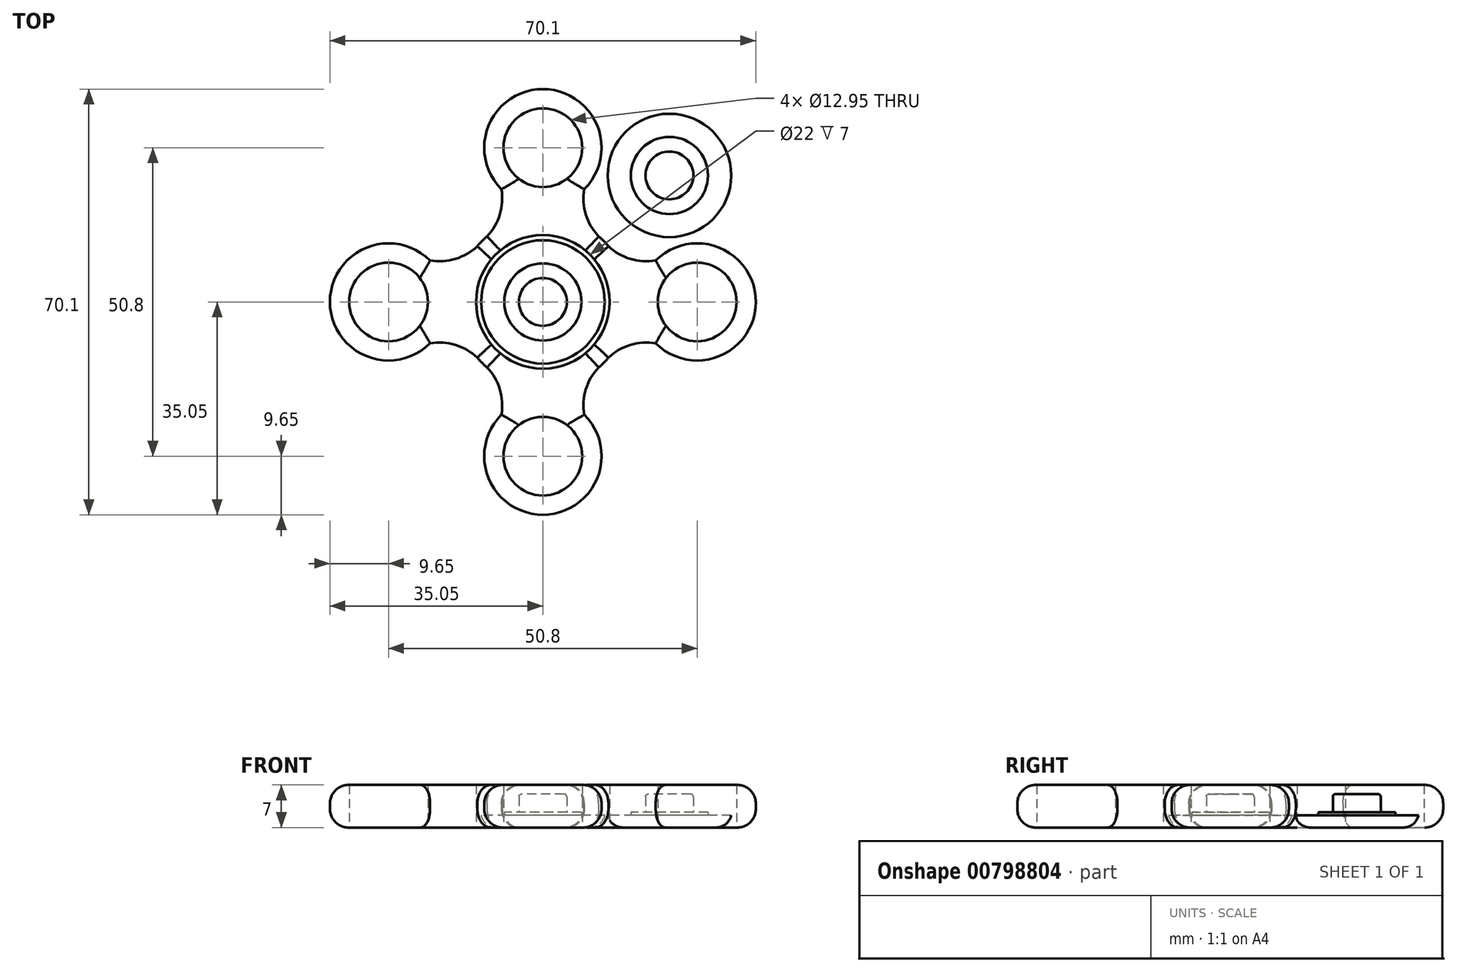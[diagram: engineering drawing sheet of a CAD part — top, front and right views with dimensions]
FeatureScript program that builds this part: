
annotation { "Feature Type Name" : "Feature", "Feature Type Description" : "" }
export const myFeature = defineFeature(function(context is Context, id is Id, definition is map)
    precondition{}
    {
        {
            var Q0;
            Q0=qCreatedBy(makeId("Top.planeOp"),FACE);
            var sketch = newSketch(context, id + "F0", { "sketchPlane" : qUnion([Q0])});
            skCircle(sketch, "E0", {"center": v(0, 0) * mm, "radius": 11 * mm});
            skCircle(sketch, "E1", {"center": v(0, 25.4) * mm, "radius": 6.48 * mm});
            skCircle(sketch, "E2", {"center": v(0, 0) * mm, "radius": 14.17 * mm});
            skCircle(sketch, "E3", {"center": v(0, 25.4) * mm, "radius": 9.65 * mm});
            skArc(sketch, "E4", {"start": v(-10.02, 10.02) * mm, "mid": v(-7.26, 13.86) * mm, "end": v(-6.82, 18.58) * mm});
            skArc(sketch, "E5", {"start": v(6.82, 18.58) * mm, "mid": v(7.26, 13.86) * mm, "end": v(10.02, 10.02) * mm});
            skCircle(sketch, "E6.1.0", {"center": v(-25.4, 0) * mm, "radius": 6.48 * mm});
            skCircle(sketch, "E6.1.1", {"center": v(-25.4, 0) * mm, "radius": 9.65 * mm});
            skArc(sketch, "E6.1.2", {"start": v(-18.58, 6.82) * mm, "mid": v(-13.86, 7.26) * mm, "end": v(-10.02, 10.02) * mm});
            skArc(sketch, "E6.1.3", {"start": v(-10.02, -10.02) * mm, "mid": v(-13.86, -7.26) * mm, "end": v(-18.58, -6.82) * mm});
            skCircle(sketch, "E6.2.0", {"center": v(0, -25.4) * mm, "radius": 6.48 * mm});
            skCircle(sketch, "E6.2.1", {"center": v(0, -25.4) * mm, "radius": 9.65 * mm});
            skArc(sketch, "E6.2.2", {"start": v(-6.82, -18.58) * mm, "mid": v(-7.26, -13.86) * mm, "end": v(-10.02, -10.02) * mm});
            skArc(sketch, "E6.2.3", {"start": v(10.02, -10.02) * mm, "mid": v(7.26, -13.86) * mm, "end": v(6.82, -18.58) * mm});
            skCircle(sketch, "E7.2.3.0", {"center": v(25.4, 0) * mm, "radius": 9.65 * mm});
            skArc(sketch, "E7.4.3.0", {"start": v(18.58, -6.82) * mm, "mid": v(13.86, -7.26) * mm, "end": v(10.02, -10.02) * mm});
            skArc(sketch, "E7.8.3.0", {"start": v(10.02, 10.02) * mm, "mid": v(13.86, 7.26) * mm, "end": v(18.58, 6.82) * mm});
            skCircle(sketch, "E7.10.3.0", {"center": v(25.4, 0) * mm, "radius": 6.48 * mm});
            skSolve(sketch);
        }
        {
            var Q0;
            Q0=qCreatedBy(makeId("Top.planeOp"),FACE);
            var sketch = newSketch(context, id + "F1", { "sketchPlane" : qUnion([Q0])});
            skCircle(sketch, "E8", {"center": v(0, 0) * mm, "radius": 10.16 * mm});
            skCircle(sketch, "E9", {"center": v(0, 0) * mm, "radius": 6.35 * mm});
            skCircle(sketch, "E10", {"center": v(0, 0) * mm, "radius": 3.94 * mm});
            skSolve(sketch);
        }
        {
            var Q0;
            Q0 = qSketchRegion(id + "F1", true);
            extrude(context, id + "F2", {"entities" : qUnion([Q0]), "depth" : 1.98 * mm, "offsetDistance" : 25.4 * mm});
        }
        {
            var Q0;
            Q0=makeQuery(id+"F1.imprint","IMPRINT",FACE,{"disambiguationData":[TD([[makeQuery(id+"F1.imprint","IMPRINT",EDGE,{"derivedFrom":sQuery(id+"F1.wireOp",EDGE,"E9")}),1.0]])]});
            extrude(context, id + "F3", {"entities" : qUnion([Q0]), "operationType" : NewBodyOperationType.ADD, "depth" : 2.5 * mm, "offsetDistance" : 25.4 * mm});
        }
        {
            var Q0;
            Q0=makeQuery(id+"F1.imprint","IMPRINT",FACE,{"disambiguationData":[TD([[makeQuery(id+"F1.imprint","IMPRINT",EDGE,{"derivedFrom":sQuery(id+"F1.wireOp",EDGE,"E10")}),1.0]])]});
            extrude(context, id + "F4", {"entities" : qUnion([Q0]), "operationType" : NewBodyOperationType.ADD, "depth" : 5.5 * mm, "offsetDistance" : 25.4 * mm});
        }
        {
            var Q0;
            {var subQ0=sQuery(id+"F1.wireOp",EDGE,"E10");var subQ1=sQuery(id+"F1.wireOp",EDGE,"E9");Q0=makeQuery(id+"F4.boolean.opBoolean","MERGE",FACE,{"derivedFrom":[makeQuery(id+"F3.boolean.opBoolean","MERGE",FACE,{"derivedFrom":[makeQuery(id+"F2.opExtrude","CAP_FACE",FACE,{"disambiguationData":[OSD([sQuery(id+"F1.wireOp",EDGE,"E8"),subQ1])],"isStart":true}),makeQuery(id+"F3.opExtrude","CAP_FACE",FACE,{"disambiguationData":[OSD([subQ1,subQ0])],"isStart":true})]}),makeQuery(id+"F4.opExtrude","CAP_FACE",FACE,{"disambiguationData":[OSD([subQ0])],"isStart":true})]});}
            fillet(context, id + "F5", {"entities" : qUnion([Q0]), "radius" : 2.54 * mm, "tangentPropagation" : true, "allowEdgeOverflow" : false});
        }
        {
            var Q0;
            Q0=makeQuery(id+"F4.opExtrude","CAP_EDGE",EDGE,{"disambiguationData":[OSD([sQuery(id+"F1.wireOp",EDGE,"E10")])],"isStart":false});
            fillet(context, id + "F6", {"entities" : qUnion([Q0]), "radius" : 0.43 * mm, "tangentPropagation" : true, "allowEdgeOverflow" : false});
        }
        {
            var Q0;
            Q0=makeQuery(id+"F2.opExtrude","SWEPT_BODY",BODY,{"disambiguationData":[OSD([sQuery(id+"F1.wireOp",EDGE,"E8"),sQuery(id+"F1.wireOp",EDGE,"E9")])]});
            transform(context, id + "F7", {"entities" : qUnion([Q0]), "transformType" : TransformType.TRANSLATION_3D, "dx" : 20.83 * mm, "dy" : 20.83 * mm, "dz" : 0 * mm, "makeCopy" : true});
        }
        {
            var Q0;
            Q0 = qSketchRegion(id + "F0", true);
            var Q1;
            Q1=makeQuery(id+"F0.imprint","IMPRINT",FACE,{"disambiguationData":[TD([[makeQuery(id+"F0.imprint","IMPRINT",EDGE,{"derivedFrom":sQuery(id+"F0.wireOp",EDGE,"E0")}),-1.0]])]});
            var Q2;
            {var subQ0=sQuery(id+"F0.wireOp",EDGE,"E6.2.2");var subQ1=sQuery(id+"F0.wireOp",EDGE,"E2");var subQ2=makeQuery(id+"F0.imprint","INTERSECT",VERTEX,{"disambiguationData":[OD(0.0)],"derivedFrom":[subQ1,subQ0]});Q2=makeQuery(id+"F0.imprint","IMPRINT",FACE,{"disambiguationData":[TD([[makeQuery(id+"F0.imprint","IMPRINT",EDGE,{"disambiguationData":[TD([[subQ2,-1.0]])],"derivedFrom":subQ1}),1.0]])]});}
            var Q3;
            {var subQ0=sQuery(id+"F0.wireOp",EDGE,"E6.1.3");var subQ1=sQuery(id+"F0.wireOp",EDGE,"E2");var subQ2=makeQuery(id+"F0.imprint","INTERSECT",VERTEX,{"disambiguationData":[OD(0.0)],"derivedFrom":[subQ1,subQ0]});Q3=makeQuery(id+"F0.imprint","IMPRINT",FACE,{"disambiguationData":[TD([[makeQuery(id+"F0.imprint","IMPRINT",EDGE,{"disambiguationData":[TD([[subQ2,1.0]])],"derivedFrom":subQ1}),1.0]])]});}
            var Q4;
            {var subQ0=sQuery(id+"F0.wireOp",EDGE,"E4");var subQ1=sQuery(id+"F0.wireOp",EDGE,"E2");var subQ2=makeQuery(id+"F0.imprint","INTERSECT",VERTEX,{"disambiguationData":[OD(0.0)],"derivedFrom":[subQ1,subQ0]});Q4=makeQuery(id+"F0.imprint","IMPRINT",FACE,{"disambiguationData":[TD([[makeQuery(id+"F0.imprint","IMPRINT",EDGE,{"disambiguationData":[TD([[subQ2,1.0]])],"derivedFrom":subQ1}),1.0]])]});}
            var Q5;
            {var subQ0=sQuery(id+"F0.wireOp",EDGE,"E6.1.2");var subQ1=sQuery(id+"F0.wireOp",EDGE,"E2");var subQ2=makeQuery(id+"F0.imprint","INTERSECT",VERTEX,{"disambiguationData":[OD(0.0)],"derivedFrom":[subQ1,subQ0]});Q5=makeQuery(id+"F0.imprint","IMPRINT",FACE,{"disambiguationData":[TD([[makeQuery(id+"F0.imprint","IMPRINT",EDGE,{"disambiguationData":[TD([[subQ2,-1.0]])],"derivedFrom":subQ1}),1.0]])]});}
            var Q6;
            {var subQ0=sQuery(id+"F0.wireOp",EDGE,"72b59728-25a7-4883-97bf-26ef1e4bd6ed.8.4.0");var subQ1=sQuery(id+"F0.wireOp",EDGE,"E2");var subQ2=makeQuery(id+"F0.imprint","INTERSECT",VERTEX,{"disambiguationData":[OD(0.0)],"derivedFrom":[subQ1,subQ0]});Q6=makeQuery(id+"F0.imprint","IMPRINT",FACE,{"disambiguationData":[TD([[makeQuery(id+"F0.imprint","IMPRINT",EDGE,{"disambiguationData":[TD([[subQ2,1.0]])],"derivedFrom":subQ1}),1.0]])]});}
            var Q7;
            {var subQ0=sQuery(id+"F0.wireOp",EDGE,"E5");var subQ1=sQuery(id+"F0.wireOp",EDGE,"E2");var subQ2=makeQuery(id+"F0.imprint","INTERSECT",VERTEX,{"disambiguationData":[OD(0.0)],"derivedFrom":[subQ1,subQ0]});Q7=makeQuery(id+"F0.imprint","IMPRINT",FACE,{"disambiguationData":[TD([[makeQuery(id+"F0.imprint","IMPRINT",EDGE,{"disambiguationData":[TD([[subQ2,-1.0]])],"derivedFrom":subQ1}),1.0]])]});}
            var Q8;
            {var subQ0=sQuery(id+"F0.wireOp",EDGE,"72b59728-25a7-4883-97bf-26ef1e4bd6ed.4.4.0");var subQ1=sQuery(id+"F0.wireOp",EDGE,"E2");var subQ2=makeQuery(id+"F0.imprint","INTERSECT",VERTEX,{"disambiguationData":[OD(0.0)],"derivedFrom":[subQ1,subQ0]});Q8=makeQuery(id+"F0.imprint","IMPRINT",FACE,{"disambiguationData":[TD([[makeQuery(id+"F0.imprint","IMPRINT",EDGE,{"disambiguationData":[TD([[subQ2,-1.0]])],"derivedFrom":subQ1}),1.0]])]});}
            var Q9;
            {var subQ0=sQuery(id+"F0.wireOp",EDGE,"E7.8.3.0");var subQ1=sQuery(id+"F0.wireOp",EDGE,"E2");var subQ2=makeQuery(id+"F0.imprint","INTERSECT",VERTEX,{"disambiguationData":[OD(0.0)],"derivedFrom":[subQ1,subQ0]});Q9=makeQuery(id+"F0.imprint","IMPRINT",FACE,{"disambiguationData":[TD([[makeQuery(id+"F0.imprint","IMPRINT",EDGE,{"disambiguationData":[TD([[subQ2,1.0]])],"derivedFrom":subQ1}),1.0]])]});}
            var Q10;
            {var subQ0=sQuery(id+"F0.wireOp",EDGE,"E7.4.3.0");var subQ1=sQuery(id+"F0.wireOp",EDGE,"E2");var subQ2=makeQuery(id+"F0.imprint","INTERSECT",VERTEX,{"disambiguationData":[OD(0.0)],"derivedFrom":[subQ1,subQ0]});Q10=makeQuery(id+"F0.imprint","IMPRINT",FACE,{"disambiguationData":[TD([[makeQuery(id+"F0.imprint","IMPRINT",EDGE,{"disambiguationData":[TD([[subQ2,-1.0]])],"derivedFrom":subQ1}),1.0]])]});}
            var Q11;
            {var subQ0=sQuery(id+"F0.wireOp",EDGE,"E6.2.3");var subQ1=sQuery(id+"F0.wireOp",EDGE,"E2");var subQ2=makeQuery(id+"F0.imprint","INTERSECT",VERTEX,{"disambiguationData":[OD(0.0)],"derivedFrom":[subQ1,subQ0]});Q11=makeQuery(id+"F0.imprint","IMPRINT",FACE,{"disambiguationData":[TD([[makeQuery(id+"F0.imprint","IMPRINT",EDGE,{"disambiguationData":[TD([[subQ2,1.0]])],"derivedFrom":subQ1}),1.0]])]});}
            extrude(context, id + "F8", {"entities" : qUnion([Q0, Q1, Q2, Q3, Q4, Q5, Q6, Q7, Q8, Q9, Q10, Q11]), "depth" : 7 * mm, "offsetDistance" : 25.4 * mm});
        }
        {
            var Q0;
            Q0=makeQuery(id+"F8.opExtrude","CAP_EDGE",EDGE,{"disambiguationData":[OSD([sQuery(id+"F0.wireOp",EDGE,"E3")])],"isStart":false});
            var Q1;
            Q1=makeQuery(id+"F8.opExtrude","CAP_EDGE",EDGE,{"disambiguationData":[OSD([sQuery(id+"F0.wireOp",EDGE,"E5")])],"isStart":false});
            var Q2;
            {var subQ0=sQuery(id+"F0.wireOp",EDGE,"E7.8.3.0");var subQ1=sQuery(id+"F0.wireOp",EDGE,"E5");var subQ2=sQuery(id+"F0.wireOp",EDGE,"E2");Q2=makeQuery(id+"F8.opExtrude","CAP_EDGE",EDGE,{"disambiguationData":[OSD([subQ2]),TDD([makeQuery(id+"F0.imprint","IMPRINT",EDGE,{"disambiguationData":[TD([[makeQuery(id+"F0.imprint","INTERSECT",VERTEX,{"derivedFrom":[subQ2,subQ0]}),-1.0]])],"derivedFrom":subQ2}),makeQuery(id+"F0.imprint","IMPRINT",EDGE,{"disambiguationData":[TD([[makeQuery(id+"F0.imprint","INTERSECT",VERTEX,{"derivedFrom":[subQ2,subQ1]}),1.0]])],"derivedFrom":subQ2})])],"isStart":false});}
            var Q3;
            Q3=makeQuery(id+"F8.opExtrude","CAP_EDGE",EDGE,{"disambiguationData":[OSD([sQuery(id+"F0.wireOp",EDGE,"E7.8.3.0")])],"isStart":false});
            var Q4;
            Q4=makeQuery(id+"F8.opExtrude","CAP_EDGE",EDGE,{"disambiguationData":[OSD([sQuery(id+"F0.wireOp",EDGE,"E7.2.3.0")])],"isStart":false});
            var Q5;
            Q5=makeQuery(id+"F8.opExtrude","CAP_EDGE",EDGE,{"disambiguationData":[OSD([sQuery(id+"F0.wireOp",EDGE,"E7.4.3.0")])],"isStart":false});
            var Q6;
            {var subQ0=sQuery(id+"F0.wireOp",EDGE,"E7.4.3.0");var subQ1=sQuery(id+"F0.wireOp",EDGE,"E6.2.3");var subQ2=sQuery(id+"F0.wireOp",EDGE,"E2");Q6=makeQuery(id+"F8.opExtrude","CAP_EDGE",EDGE,{"disambiguationData":[OSD([subQ2]),TDD([makeQuery(id+"F0.imprint","IMPRINT",EDGE,{"disambiguationData":[TD([[makeQuery(id+"F0.imprint","INTERSECT",VERTEX,{"derivedFrom":[subQ2,subQ1]}),-1.0]])],"derivedFrom":subQ2}),makeQuery(id+"F0.imprint","IMPRINT",EDGE,{"disambiguationData":[TD([[makeQuery(id+"F0.imprint","INTERSECT",VERTEX,{"derivedFrom":[subQ2,subQ0]}),1.0]])],"derivedFrom":subQ2})])],"isStart":false});}
            var Q7;
            Q7=makeQuery(id+"F8.opExtrude","CAP_EDGE",EDGE,{"disambiguationData":[OSD([sQuery(id+"F0.wireOp",EDGE,"E6.2.3")])],"isStart":false});
            var Q8;
            Q8=makeQuery(id+"F8.opExtrude","CAP_EDGE",EDGE,{"disambiguationData":[OSD([sQuery(id+"F0.wireOp",EDGE,"E6.2.1")])],"isStart":false});
            var Q9;
            Q9=makeQuery(id+"F8.opExtrude","CAP_EDGE",EDGE,{"disambiguationData":[OSD([sQuery(id+"F0.wireOp",EDGE,"E6.2.2")])],"isStart":false});
            var Q10;
            {var subQ0=sQuery(id+"F0.wireOp",EDGE,"E6.2.2");var subQ1=sQuery(id+"F0.wireOp",EDGE,"E6.1.3");var subQ2=sQuery(id+"F0.wireOp",EDGE,"E2");Q10=makeQuery(id+"F8.opExtrude","CAP_EDGE",EDGE,{"disambiguationData":[OSD([subQ2]),TDD([makeQuery(id+"F0.imprint","IMPRINT",EDGE,{"disambiguationData":[TD([[makeQuery(id+"F0.imprint","INTERSECT",VERTEX,{"derivedFrom":[subQ2,subQ1]}),-1.0]])],"derivedFrom":subQ2}),makeQuery(id+"F0.imprint","IMPRINT",EDGE,{"disambiguationData":[TD([[makeQuery(id+"F0.imprint","INTERSECT",VERTEX,{"derivedFrom":[subQ2,subQ0]}),1.0]])],"derivedFrom":subQ2})])],"isStart":false});}
            var Q11;
            Q11=makeQuery(id+"F8.opExtrude","CAP_EDGE",EDGE,{"disambiguationData":[OSD([sQuery(id+"F0.wireOp",EDGE,"E6.1.3")])],"isStart":false});
            var Q12;
            Q12=makeQuery(id+"F8.opExtrude","CAP_EDGE",EDGE,{"disambiguationData":[OSD([sQuery(id+"F0.wireOp",EDGE,"E6.1.1")])],"isStart":false});
            var Q13;
            Q13=makeQuery(id+"F8.opExtrude","CAP_EDGE",EDGE,{"disambiguationData":[OSD([sQuery(id+"F0.wireOp",EDGE,"E6.1.2")])],"isStart":false});
            var Q14;
            {var subQ0=sQuery(id+"F0.wireOp",EDGE,"E6.1.2");var subQ1=sQuery(id+"F0.wireOp",EDGE,"E4");var subQ2=sQuery(id+"F0.wireOp",EDGE,"E2");Q14=makeQuery(id+"F8.opExtrude","CAP_EDGE",EDGE,{"disambiguationData":[OSD([subQ2]),TDD([makeQuery(id+"F0.imprint","IMPRINT",EDGE,{"disambiguationData":[TD([[makeQuery(id+"F0.imprint","INTERSECT",VERTEX,{"derivedFrom":[subQ2,subQ1]}),-1.0]])],"derivedFrom":subQ2}),makeQuery(id+"F0.imprint","IMPRINT",EDGE,{"disambiguationData":[TD([[makeQuery(id+"F0.imprint","INTERSECT",VERTEX,{"derivedFrom":[subQ2,subQ0]}),1.0]])],"derivedFrom":subQ2})])],"isStart":false});}
            var Q15;
            Q15=makeQuery(id+"F8.opExtrude","CAP_EDGE",EDGE,{"disambiguationData":[OSD([sQuery(id+"F0.wireOp",EDGE,"E4")])],"isStart":false});
            var Q16;
            Q16=makeQuery(id+"F8.opExtrude","CAP_EDGE",EDGE,{"disambiguationData":[OSD([sQuery(id+"F0.wireOp",EDGE,"E3")])],"isStart":true});
            var Q17;
            Q17=makeQuery(id+"F8.opExtrude","CAP_EDGE",EDGE,{"disambiguationData":[OSD([sQuery(id+"F0.wireOp",EDGE,"E4")])],"isStart":true});
            var Q18;
            {var subQ0=sQuery(id+"F0.wireOp",EDGE,"E6.1.2");var subQ1=sQuery(id+"F0.wireOp",EDGE,"E4");var subQ2=sQuery(id+"F0.wireOp",EDGE,"E2");Q18=makeQuery(id+"F8.opExtrude","CAP_EDGE",EDGE,{"disambiguationData":[OSD([subQ2]),TDD([makeQuery(id+"F0.imprint","IMPRINT",EDGE,{"disambiguationData":[TD([[makeQuery(id+"F0.imprint","INTERSECT",VERTEX,{"derivedFrom":[subQ2,subQ1]}),-1.0]])],"derivedFrom":subQ2}),makeQuery(id+"F0.imprint","IMPRINT",EDGE,{"disambiguationData":[TD([[makeQuery(id+"F0.imprint","INTERSECT",VERTEX,{"derivedFrom":[subQ2,subQ0]}),1.0]])],"derivedFrom":subQ2})])],"isStart":true});}
            var Q19;
            Q19=makeQuery(id+"F8.opExtrude","CAP_EDGE",EDGE,{"disambiguationData":[OSD([sQuery(id+"F0.wireOp",EDGE,"E6.1.2")])],"isStart":true});
            var Q20;
            Q20=makeQuery(id+"F8.opExtrude","CAP_EDGE",EDGE,{"disambiguationData":[OSD([sQuery(id+"F0.wireOp",EDGE,"E6.1.1")])],"isStart":true});
            var Q21;
            Q21=makeQuery(id+"F8.opExtrude","CAP_EDGE",EDGE,{"disambiguationData":[OSD([sQuery(id+"F0.wireOp",EDGE,"E5")])],"isStart":true});
            var Q22;
            {var subQ0=sQuery(id+"F0.wireOp",EDGE,"E7.8.3.0");var subQ1=sQuery(id+"F0.wireOp",EDGE,"E5");var subQ2=sQuery(id+"F0.wireOp",EDGE,"E2");Q22=makeQuery(id+"F8.opExtrude","CAP_EDGE",EDGE,{"disambiguationData":[OSD([subQ2]),TDD([makeQuery(id+"F0.imprint","IMPRINT",EDGE,{"disambiguationData":[TD([[makeQuery(id+"F0.imprint","INTERSECT",VERTEX,{"derivedFrom":[subQ2,subQ0]}),-1.0]])],"derivedFrom":subQ2}),makeQuery(id+"F0.imprint","IMPRINT",EDGE,{"disambiguationData":[TD([[makeQuery(id+"F0.imprint","INTERSECT",VERTEX,{"derivedFrom":[subQ2,subQ1]}),1.0]])],"derivedFrom":subQ2})])],"isStart":true});}
            var Q23;
            Q23=makeQuery(id+"F8.opExtrude","CAP_EDGE",EDGE,{"disambiguationData":[OSD([sQuery(id+"F0.wireOp",EDGE,"E7.8.3.0")])],"isStart":true});
            var Q24;
            Q24=makeQuery(id+"F8.opExtrude","CAP_EDGE",EDGE,{"disambiguationData":[OSD([sQuery(id+"F0.wireOp",EDGE,"E7.2.3.0")])],"isStart":true});
            var Q25;
            Q25=makeQuery(id+"F8.opExtrude","CAP_EDGE",EDGE,{"disambiguationData":[OSD([sQuery(id+"F0.wireOp",EDGE,"E7.4.3.0")])],"isStart":true});
            var Q26;
            {var subQ0=sQuery(id+"F0.wireOp",EDGE,"E7.4.3.0");var subQ1=sQuery(id+"F0.wireOp",EDGE,"E6.2.3");var subQ2=sQuery(id+"F0.wireOp",EDGE,"E2");Q26=makeQuery(id+"F8.opExtrude","CAP_EDGE",EDGE,{"disambiguationData":[OSD([subQ2]),TDD([makeQuery(id+"F0.imprint","IMPRINT",EDGE,{"disambiguationData":[TD([[makeQuery(id+"F0.imprint","INTERSECT",VERTEX,{"derivedFrom":[subQ2,subQ1]}),-1.0]])],"derivedFrom":subQ2}),makeQuery(id+"F0.imprint","IMPRINT",EDGE,{"disambiguationData":[TD([[makeQuery(id+"F0.imprint","INTERSECT",VERTEX,{"derivedFrom":[subQ2,subQ0]}),1.0]])],"derivedFrom":subQ2})])],"isStart":true});}
            var Q27;
            Q27=makeQuery(id+"F8.opExtrude","CAP_EDGE",EDGE,{"disambiguationData":[OSD([sQuery(id+"F0.wireOp",EDGE,"E6.2.3")])],"isStart":true});
            var Q28;
            Q28=makeQuery(id+"F8.opExtrude","CAP_EDGE",EDGE,{"disambiguationData":[OSD([sQuery(id+"F0.wireOp",EDGE,"E6.2.1")])],"isStart":true});
            var Q29;
            Q29=makeQuery(id+"F8.opExtrude","CAP_EDGE",EDGE,{"disambiguationData":[OSD([sQuery(id+"F0.wireOp",EDGE,"E6.2.2")])],"isStart":true});
            var Q30;
            {var subQ0=sQuery(id+"F0.wireOp",EDGE,"E6.2.2");var subQ1=sQuery(id+"F0.wireOp",EDGE,"E6.1.3");var subQ2=sQuery(id+"F0.wireOp",EDGE,"E2");Q30=makeQuery(id+"F8.opExtrude","CAP_EDGE",EDGE,{"disambiguationData":[OSD([subQ2]),TDD([makeQuery(id+"F0.imprint","IMPRINT",EDGE,{"disambiguationData":[TD([[makeQuery(id+"F0.imprint","INTERSECT",VERTEX,{"derivedFrom":[subQ2,subQ1]}),-1.0]])],"derivedFrom":subQ2}),makeQuery(id+"F0.imprint","IMPRINT",EDGE,{"disambiguationData":[TD([[makeQuery(id+"F0.imprint","INTERSECT",VERTEX,{"derivedFrom":[subQ2,subQ0]}),1.0]])],"derivedFrom":subQ2})])],"isStart":true});}
            var Q31;
            Q31=makeQuery(id+"F8.opExtrude","CAP_EDGE",EDGE,{"disambiguationData":[OSD([sQuery(id+"F0.wireOp",EDGE,"E6.1.3")])],"isStart":true});
            fillet(context, id + "F9", {"entities" : qUnion([Q0, Q1, Q2, Q3, Q4, Q5, Q6, Q7, Q8, Q9, Q10, Q11, Q12, Q13, Q14, Q15, Q16, Q17, Q18, Q19, Q20, Q21, Q22, Q23, Q24, Q25, Q26, Q27, Q28, Q29, Q30, Q31]), "radius" : 3.05 * mm, "tangentPropagation" : true, "allowEdgeOverflow" : false});
        }
    });
